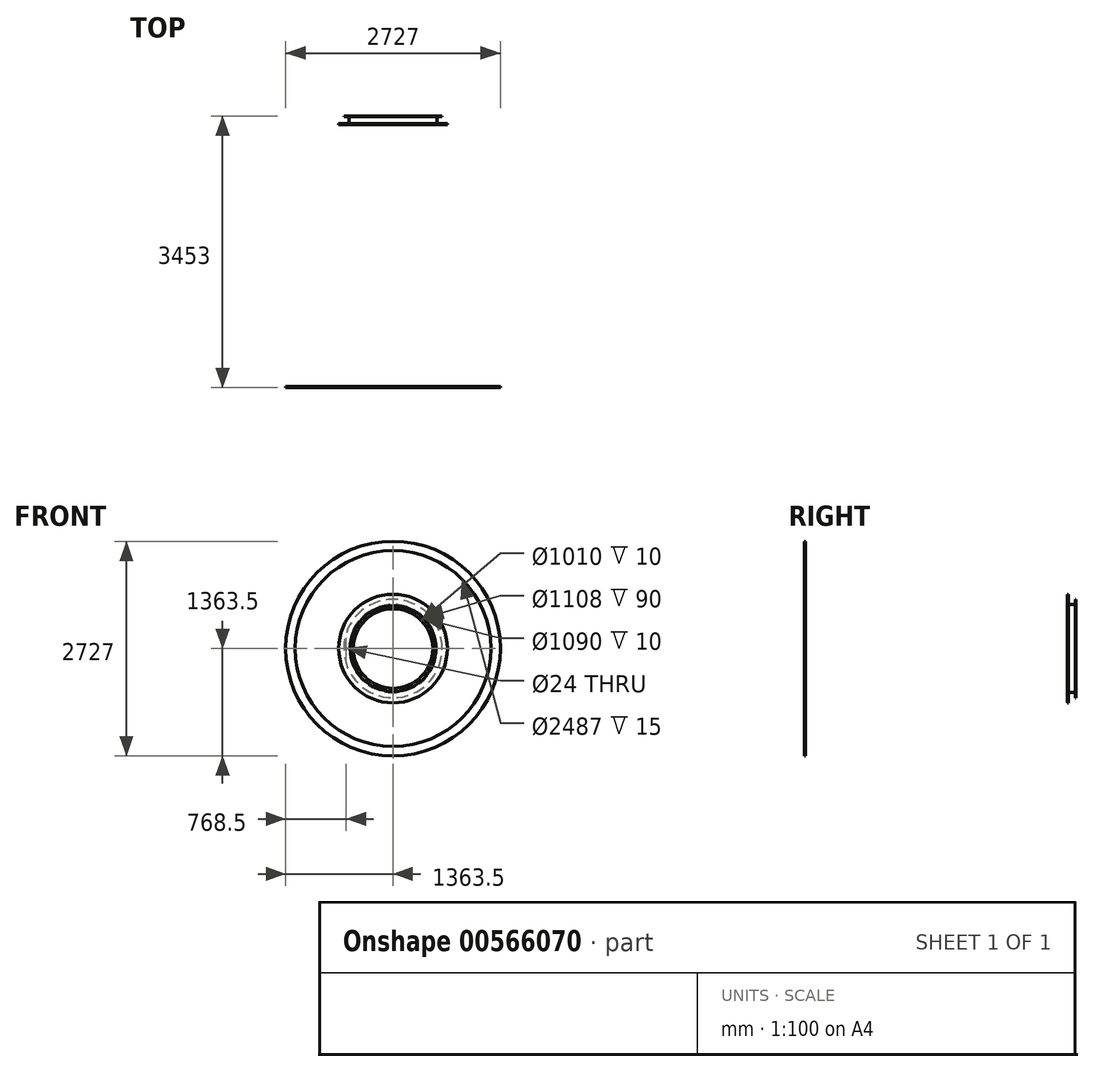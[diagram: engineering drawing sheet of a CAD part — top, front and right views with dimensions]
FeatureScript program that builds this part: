
annotation { "Feature Type Name" : "Feature", "Feature Type Description" : "" }
export const myFeature = defineFeature(function(context is Context, id is Id, definition is map)
    precondition{}
    {
        {
            var Q0;
            Q0=qCreatedBy(makeId("Front.planeOp"),FACE);
            var sketch = newSketch(context, id + "F0", { "sketchPlane" : qUnion([Q0])});
            skCircle(sketch, "E0", {"center": v(0, 0) * mm, "radius": 625 * mm});
            skCircle(sketch, "E1", {"center": v(0, 0) * mm, "radius": 505 * mm});
            skSolve(sketch);
        }
        {
            var Q0;
            Q0=qSketchRegion(id+"F0",true);
            extrude(context, id + "F1", {"entities" : qUnion([Q0]), "oppositeDirection" : true, "depth" : 10 * mm, "offsetDistance" : 25.4 * mm});
        }
        {
            var Q0;
            Q0=makeQuery(id+"F0.imprint","IMPRINT",FACE,{"disambiguationData":[TD([[makeQuery(id+"F0.imprint","IMPRINT",EDGE,{"derivedFrom":sQuery(id+"F0.wireOp",EDGE,"E0")}),1.0]])]});
            var sketch = newSketch(context, id + "F2", { "sketchPlane" : qUnion([Q0])});
            skCircle(sketch, "E2", {"center": v(0, 0) * mm, "radius": 554 * mm});
            skCircle(sketch, "E3", {"center": v(0, 0) * mm, "radius": 560 * mm});
            skSolve(sketch);
        }
        {
            var Q0;
            Q0=qSketchRegion(id+"F2",true);
            extrude(context, id + "F3", {"entities" : qUnion([Q0]), "operationType" : NewBodyOperationType.ADD, "depth" : 90 * mm, "offsetDistance" : 25 * mm});
        }
        {
            var Q0;
            Q0=makeQuery(id+"F3.opExtrude","CAP_FACE",FACE,{"disambiguationData":[OSD([sQuery(id+"F2.wireOp",EDGE,"E2"),sQuery(id+"F2.wireOp",EDGE,"E3")])],"isStart":false});
            var sketch = newSketch(context, id + "F4", { "sketchPlane" : qUnion([Q0])});
            skCircle(sketch, "E4", {"center": v(0, 0) * mm, "radius": 690 * mm});
            skCircle(sketch, "E5", {"center": v(0, 0) * mm, "radius": 545 * mm});
            skSolve(sketch);
        }
        {
            var Q0;
            Q0=qSketchRegion(id+"F4",true);
            extrude(context, id + "F5", {"entities" : qUnion([Q0]), "operationType" : NewBodyOperationType.ADD, "depth" : 10 * mm, "offsetDistance" : 25 * mm});
        }
        {
            var Q0;
            Q0=makeQuery(id+"F1.opExtrude","CAP_FACE",FACE,{"disambiguationData":[OSD([sQuery(id+"F0.wireOp",EDGE,"E0"),sQuery(id+"F0.wireOp",EDGE,"E1")])],"isStart":false});
            cPlane(context, id + "F6", {"entities" : qUnion([Q0]), "cplaneType" : CPlaneType.OFFSET, "offset" : 3453 * mm, "oppositeDirection" : true, "width" : 150 * mm, "height" : 150 * mm});
        }
        {
            var Q0;
            Q0=qCreatedBy(id+"F6.planeOp",FACE);
            var sketch = newSketch(context, id + "F7", { "sketchPlane" : qUnion([Q0])});
            skCircle(sketch, "E6", {"center": v(0, 0) * mm, "radius": 1363.5 * mm});
            skCircle(sketch, "E7", {"center": v(0, 0) * mm, "radius": 1243.5 * mm});
            skSolve(sketch);
        }
        {
            var Q0;
            Q0=qSketchRegion(id+"F7",true);
            extrude(context, id + "F8", {"entities" : qUnion([Q0]), "depth" : 15 * mm, "offsetDistance" : 25 * mm});
        }
        {
            var Q0;
            Q0=makeQuery(id+"F8.opExtrude","CAP_FACE",FACE,{"disambiguationData":[OSD([sQuery(id+"F7.wireOp",EDGE,"E6"),sQuery(id+"F7.wireOp",EDGE,"E7")])],"isStart":false});
            var sketch = newSketch(context, id + "F9", { "sketchPlane" : qUnion([Q0])});
            skCircle(sketch, "E8", {"center": v(0, 0) * mm, "radius": 1263.5 * mm});
            skSolve(sketch);
        }
        {
            var Q0;
            Q0=makeQuery(id+"F5.opExtrude","CAP_FACE",FACE,{"disambiguationData":[OSD([sQuery(id+"F4.wireOp",EDGE,"E4"),sQuery(id+"F4.wireOp",EDGE,"E5")])],"isStart":false});
            var sketch = newSketch(context, id + "F10", { "sketchPlane" : qUnion([Q0])});
            skCircle(sketch, "E9", {"center": v(0, 0) * mm, "radius": 674 * mm});
            skSolve(sketch);
        }
        {
            var Q0;
            Q0=makeQuery(id+"F9.imprint","IMPRINT",FACE,{"disambiguationData":[TD([[makeQuery(id+"F9.imprint","IMPRINT",EDGE,{"derivedFrom":sQuery(id+"F9.wireOp",EDGE,"E8")}),-1.0]])]});
            var sketch = newSketch(context, id + "F11", { "sketchPlane" : qUnion([Q0])});
            skCircle(sketch, "E10", {"center": v(0, 0) * mm, "radius": 1257.5 * mm});
            skSolve(sketch);
        }
        {
            var Q0;
            Q0=makeQuery(id+"F10.imprint","IMPRINT",FACE,{"disambiguationData":[TD([[makeQuery(id+"F10.imprint","IMPRINT",EDGE,{"derivedFrom":sQuery(id+"F10.wireOp",EDGE,"E9")}),1.0]])]});
            var sketch = newSketch(context, id + "F12", { "sketchPlane" : qUnion([Q0])});
            skCircle(sketch, "E11", {"center": v(0, 0) * mm, "radius": 668 * mm});
            skSolve(sketch);
        }
        {
            var Q0;
            Q0 = qSketchRegion(id + "F9", true);
            var Q1;
            Q1 = qSketchRegion(id + "F10", true);
            var Q2;
            Q2 = qConstructionFilter(qBodyType(qCreatedBy(id + "F11" ,EDGE), BodyType.WIRE), ConstructionObject.NO);
            var Q3;
            Q3 = qConstructionFilter(qBodyType(qCreatedBy(id + "F12" ,EDGE), BodyType.WIRE), ConstructionObject.NO);
            loft(context, id + "F13", {"bodyType" : ToolBodyType.SURFACE, "sheetProfilesArray" : [{ "sheetProfileEntities" : qUnion([Q0]) }, { "sheetProfileEntities" : qUnion([Q1]) }], "wireProfilesArray" : [{ "wireProfileEntities" : qUnion([Q2]) }, { "wireProfileEntities" : qUnion([Q3]) }]});
        }
        {
            var Q0;
            Q0=makeQuery(id+"F1.opExtrude","CAP_FACE",FACE,{"disambiguationData":[OSD([sQuery(id+"F0.wireOp",EDGE,"E0"),sQuery(id+"F0.wireOp",EDGE,"E1")])],"isStart":false});
            var sketch = newSketch(context, id + "F14", { "sketchPlane" : qUnion([Q0])});
            skCircle(sketch, "E12", {"center": v(595, 0) * mm, "radius": 12 * mm});
            skSolve(sketch);
        }
        {
            var Q0;
            Q0 = qSketchRegion(id + "F14", true);
            extrude(context, id + "F15", {"entities" : qUnion([Q0]), "operationType" : NewBodyOperationType.REMOVE, "endBound" : BoundingType.UP_TO_NEXT, "oppositeDirection" : true, "depth" : 25 * mm, "offsetDistance" : 25 * mm});
        }
    });
